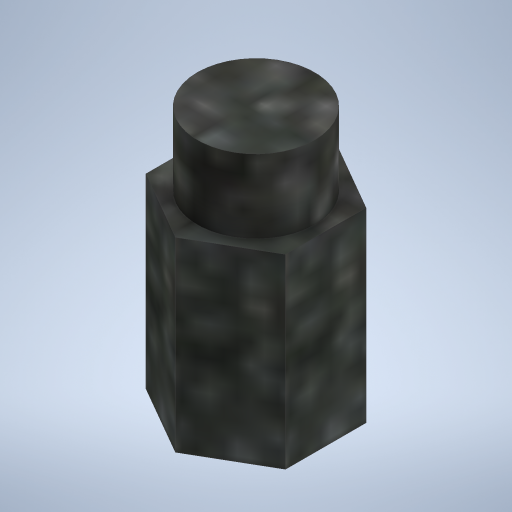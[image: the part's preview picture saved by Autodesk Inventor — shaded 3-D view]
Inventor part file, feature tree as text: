
AUTODESK INVENTOR PART (.ipt)
format: ipt  version: 2023 (Build 270158030, 158C)  size: 310,784 bytes
history: native  units: in
note: dims shown in document units (in); Inventor stores cm internally (conversion verified against a paired STEP export)
features: extrude x2, sketch x2
ambient origin geometry x8: Origin, YZ Plane, XZ Plane, XY Plane, X Axis, Y Axis, Z Axis, Center Point
bodies: Solid1 (feature_tree)
feature tree (4):
  extrude  "Extrusion1"  Depth=0.5in TaperAngle=0.0deg
  extrude  "Extrusion2"  Depth=0.1969in TaperAngle=0.0deg
  sketch  "Sketch1"  dims[d0=0.375in d1=0.5in d2=0.0in]
  sketch  "Sketch2"  dims[d3=0.315in d4=0.1969in d5=0.0in d11=0.835in d12=0.0in]
